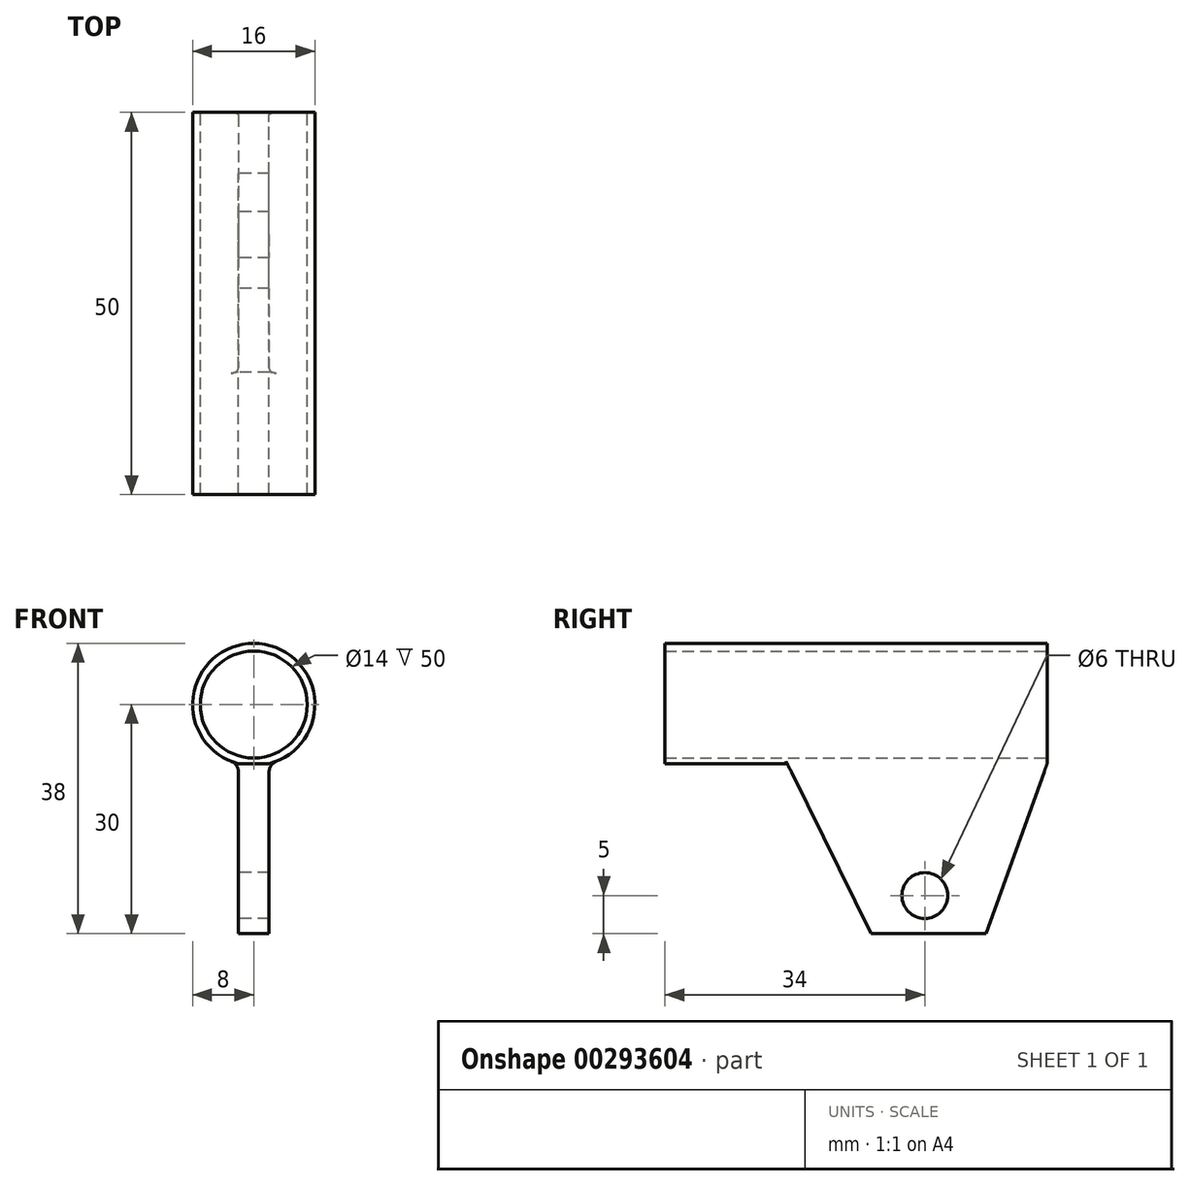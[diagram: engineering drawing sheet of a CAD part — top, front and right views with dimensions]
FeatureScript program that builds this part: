
annotation { "Feature Type Name" : "Feature", "Feature Type Description" : "" }
export const myFeature = defineFeature(function(context is Context, id is Id, definition is map)
    precondition{}
    {
        {
            var Q0;
            Q0=qCreatedBy(makeId("Front.planeOp"),FACE);
            var sketch = newSketch(context, id + "F0", { "sketchPlane" : qUnion([Q0])});
            skArc(sketch, "E0", {"start": v(2, -7.75) * mm, "mid": v(0, 8) * mm, "end": v(-2, -7.75) * mm});
            skCircle(sketch, "E1", {"center": v(0, 0) * mm, "radius": 7 * mm});
            skLineSegment(sketch, "E2", {"start": v(2, -7.75) * mm, "end": v(2, -30) * mm});
            skLineSegment(sketch, "E3", {"start": v(2, -30) * mm, "end": v(0, -30) * mm});
            skLineSegment(sketch, "E4", {"start": v(0, 0) * mm, "end": v(0, -21.9) * mm, "construction": true});
            skLineSegment(sketch, "E5.MirrorCS", {"start": v(-2, -30) * mm, "end": v(0, -30) * mm});
            skLineSegment(sketch, "E6.MirrorCS", {"start": v(-2, -7.75) * mm, "end": v(-2, -30) * mm});
            skSolve(sketch);
        }
        {
            var Q0;
            Q0=makeQuery(id+"F0.imprint","IMPRINT",FACE,{"disambiguationData":[TD([[makeQuery(id+"F0.imprint","IMPRINT",EDGE,{"derivedFrom":sQuery(id+"F0.wireOp",EDGE,"E0")}),1.0]])]});
            extrude(context, id + "F1", {"entities" : qUnion([Q0]), "depth" : 50 * mm});
        }
        {
            var Q0;
            Q0=qCreatedBy(makeId("Top.planeOp"),FACE);
            var sketch = newSketch(context, id + "F2", { "sketchPlane" : qUnion([Q0])});
            skLineSegment(sketch, "E7", {"start": v(8, 0) * mm, "end": v(8, -50) * mm});
            skLineSegment(sketch, "E8", {"start": v(-8, -50) * mm, "end": v(-8, 0) * mm});
            skLineSegment(sketch, "E9.0", {"start": v(8, 0) * mm, "end": v(-8, 0) * mm});
            skSolve(sketch);
        }
        {
            var Q0;
            Q0=makeQuery(id+"F1.opExtrude","SWEPT_FACE",FACE,{"disambiguationData":[OSD([sQuery(id+"F0.wireOp",EDGE,"E6.MirrorCS")])]});
            var sketch = newSketch(context, id + "F3", { "sketchPlane" : qUnion([Q0])});
            skLineSegment(sketch, "E10", {"start": v(34, -7.75) * mm, "end": v(23, -30) * mm});
            skLineSegment(sketch, "E11", {"start": v(0, -7.75) * mm, "end": v(8, -30) * mm});
            skCircle(sketch, "E12", {"center": v(16, -25) * mm, "radius": 3 * mm});
            skSolve(sketch);
        }
        {
            var Q0;
            {var subQ0=sQuery(id+"F3.wireOp",EDGE,"E10");Q0=makeQuery(id+"F3.imprint","IMPRINT",FACE,{"disambiguationData":[TD([[makeQuery(id+"F3.imprint","IMPRINT",EDGE,{"derivedFrom":subQ0}),1.0]])]});}
            var Q1;
            {var subQ0=sQuery(id+"F3.wireOp",EDGE,"E11");Q1=makeQuery(id+"F3.imprint","IMPRINT",FACE,{"disambiguationData":[TD([[makeQuery(id+"F3.imprint","IMPRINT",EDGE,{"derivedFrom":subQ0}),-1.0]])]});}
            var Q2;
            Q2=makeQuery(id+"F3.imprint","IMPRINT",FACE,{"disambiguationData":[TD([[makeQuery(id+"F3.imprint","IMPRINT",EDGE,{"derivedFrom":sQuery(id+"F3.wireOp",EDGE,"E12")}),1.0]])]});
            extrude(context, id + "F4", {"entities" : qUnion([Q0, Q1, Q2]), "operationType" : NewBodyOperationType.REMOVE, "oppositeDirection" : true, "depth" : 25 * mm});
        }
        {
            var Q0;
            Q0=makeQuery(id+"F4.boolean.opBoolean","SPLIT",EDGE,{"derivedFrom":makeQuery(id+"F1.opExtrude","SWEPT_EDGE",EDGE,{"disambiguationData":[OSD([sQuery(id+"F0.wireOp",EDGE,"E0"),sQuery(id+"F0.wireOp",EDGE,"E6.MirrorCS")])]})});
            var Q1;
            {var subQ0=sQuery(id+"F0.wireOp",EDGE,"E0");var subQ1=sQuery(id+"F0.wireOp",EDGE,"E2");Q1=makeQuery(id+"F4.boolean.opBoolean","SPLIT",EDGE,{"disambiguationData":[topologyDisambiguationEdgeConnected([makeQuery(id+"F1.opExtrude","SWEPT_FACE",FACE,{"disambiguationData":[OSD([subQ1])]})])],"derivedFrom":makeQuery(id+"F1.opExtrude","SWEPT_EDGE",EDGE,{"disambiguationData":[OSD([subQ0,subQ1])]})});}
            fillet(context, id + "F5", {"entities" : qUnion([Q0, Q1]), "radius" : 1.5 * mm, "tangentPropagation" : true, "allowEdgeOverflow" : false});
        }
    });
